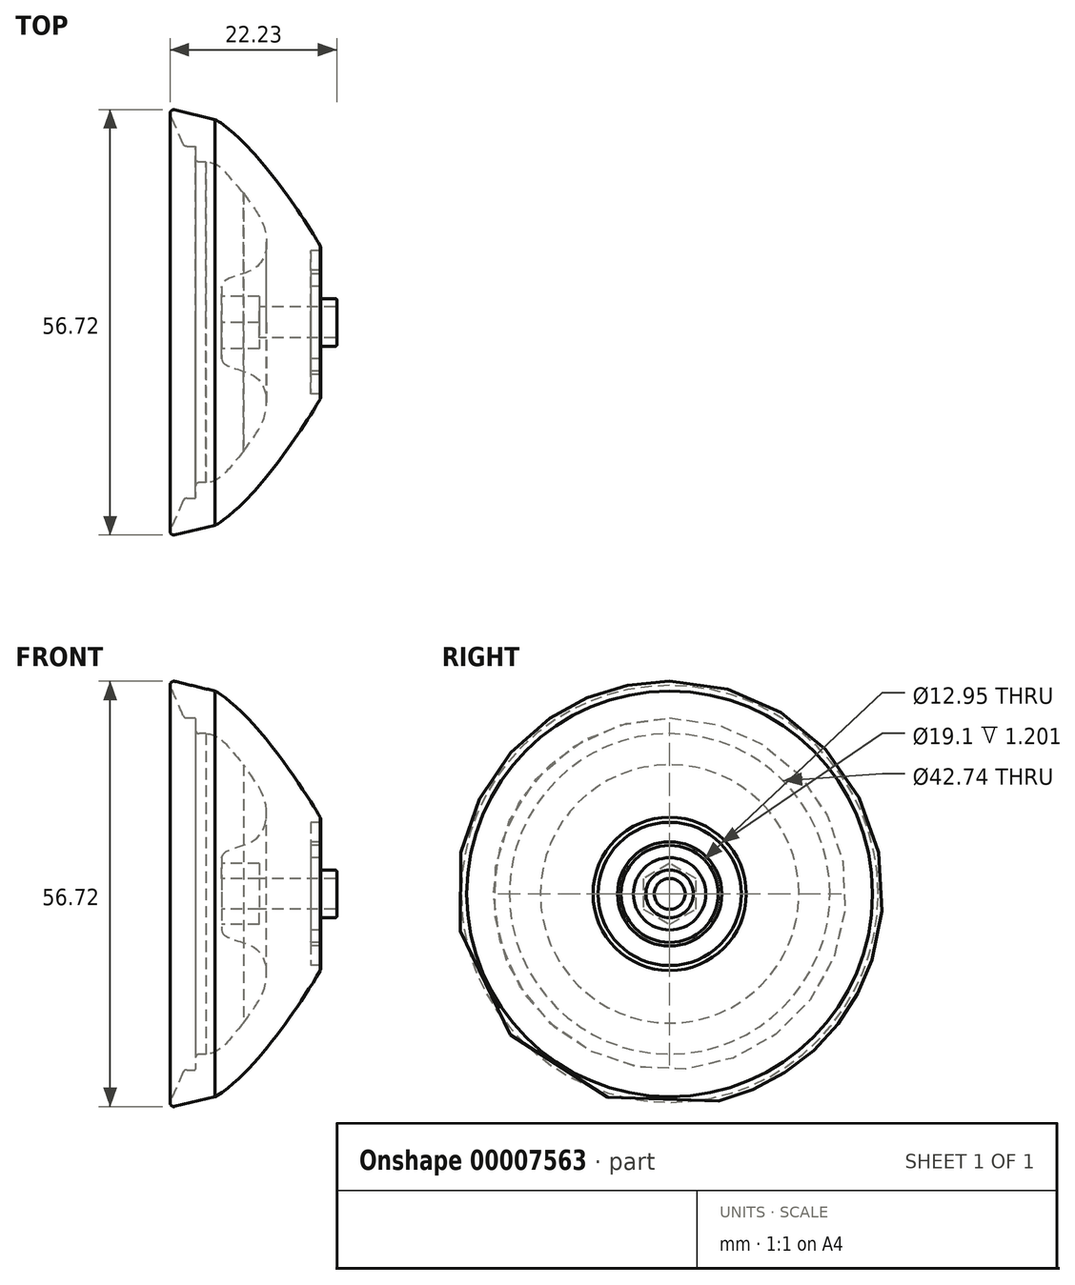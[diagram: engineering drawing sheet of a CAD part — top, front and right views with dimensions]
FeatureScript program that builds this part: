
annotation { "Feature Type Name" : "Feature", "Feature Type Description" : "" }
export const myFeature = defineFeature(function(context is Context, id is Id, definition is map)
    precondition{}
    {
        {
            var Q0;
            Q0=qCreatedBy(makeId("Front.planeOp"),FACE);
            var sketch = newSketch(context, id + "F0", { "sketchPlane" : qUnion([Q0])});
            skLineSegment(sketch, "E0", {"start": v(-27.14, 28.5) * mm, "end": v(36.68, 28.5) * mm, "construction": true});
            skLineSegment(sketch, "E1", {"start": v(20, 42.96) * mm, "end": v(20, -13.53) * mm, "construction": true});
            skLineSegment(sketch, "E2.bottom", {"start": v(22.05, 3.18) * mm, "end": v(20.1, 3.18) * mm});
            skLineSegment(sketch, "E2.left", {"start": v(22.25, 2.98) * mm, "end": v(22.25, 2.25) * mm});
            skLineSegment(sketch, "E3", {"start": v(20, 3.28) * mm, "end": v(20, 4.82) * mm});
            skLineSegment(sketch, "E4", {"start": v(20, 4.82) * mm, "end": v(18.9, 4.82) * mm});
            skLineSegment(sketch, "E5", {"start": v(18.8, 4.92) * mm, "end": v(18.8, 6.38) * mm});
            skLineSegment(sketch, "E6", {"start": v(18.9, 6.48) * mm, "end": v(20, 6.48) * mm});
            skLineSegment(sketch, "E7", {"start": v(20, 6.95) * mm, "end": v(18.8, 6.95) * mm});
            skLineSegment(sketch, "E8", {"start": v(18.8, 6.95) * mm, "end": v(18.8, 9.55) * mm});
            skLineSegment(sketch, "E9", {"start": v(18.8, 9.55) * mm, "end": v(20, 9.55) * mm});
            skLineSegment(sketch, "E10", {"start": v(6.02, 27.05) * mm, "end": v(0.64, 28.35) * mm});
            skLineSegment(sketch, "E11", {"start": v(2.24, 23.47) * mm, "end": v(3.32, 23.47) * mm});
            skLineSegment(sketch, "E12", {"start": v(3.42, 23.37) * mm, "end": v(3.42, 21.87) * mm});
            skLineSegment(sketch, "E13", {"start": v(6.92, 4.84) * mm, "end": v(6.92, 2.25) * mm});
            skLineSegment(sketch, "E14", {"start": v(6.92, 0) * mm, "end": v(6.92, 0) * mm});
            skLineSegment(sketch, "E15", {"start": v(6.92, 0) * mm, "end": v(22.25, 0) * mm});
            skLineSegment(sketch, "E16.top", {"start": v(20.1, 6.48) * mm, "end": v(20.1, 6.48) * mm});
            skLineSegment(sketch, "E16.left", {"start": v(20.1, 6.85) * mm, "end": v(20.1, 6.58) * mm});
            skLineSegment(sketch, "E17.right", {"start": v(20.1, 9.65) * mm, "end": v(20.1, 9.93) * mm});
            skLineSegment(sketch, "E18", {"start": v(3.92, 21.37) * mm, "end": v(4.8, 21.37) * mm});
            skPoint(sketch, "E19.visualSharp", {"position": v(0, 28.5) * mm});
            skArc(sketch, "E19.filletArc", {"start": v(0.64, 28.35) * mm, "mid": v(0.18, 28.23) * mm, "end": v(0.02, 27.8) * mm});
            skPoint(sketch, "E20.visualSharp", {"position": v(20.1, 10.09) * mm});
            skArc(sketch, "E20.filletArc", {"start": v(20.1, 9.93) * mm, "mid": v(20.08, 10.08) * mm, "end": v(20.02, 10.22) * mm});
            skPoint(sketch, "E21.visualSharp", {"position": v(6.92, 5.84) * mm});
            skPoint(sketch, "E22.visualSharp", {"position": v(20.1, 9.55) * mm});
            skArc(sketch, "E22.filletArc", {"start": v(20, 9.55) * mm, "mid": v(20.07, 9.58) * mm, "end": v(20.1, 9.65) * mm});
            skPoint(sketch, "E23.visualSharp", {"position": v(20.1, 6.95) * mm});
            skArc(sketch, "E23.filletArc", {"start": v(20.1, 6.85) * mm, "mid": v(20.07, 6.92) * mm, "end": v(20, 6.95) * mm});
            skPoint(sketch, "E24.visualSharp", {"position": v(20.1, 6.48) * mm});
            skArc(sketch, "E24.filletArc", {"start": v(20, 6.48) * mm, "mid": v(20.07, 6.5) * mm, "end": v(20.1, 6.58) * mm});
            skPoint(sketch, "E25.visualSharp", {"position": v(18.8, 6.48) * mm});
            skArc(sketch, "E25.filletArc", {"start": v(18.9, 6.48) * mm, "mid": v(18.83, 6.45) * mm, "end": v(18.8, 6.38) * mm});
            skPoint(sketch, "E26.visualSharp", {"position": v(18.8, 4.82) * mm});
            skArc(sketch, "E26.filletArc", {"start": v(18.8, 4.92) * mm, "mid": v(18.83, 4.85) * mm, "end": v(18.9, 4.82) * mm});
            skPoint(sketch, "E27.visualSharp", {"position": v(20, 3.18) * mm});
            skArc(sketch, "E27.filletArc", {"start": v(20, 3.28) * mm, "mid": v(20.03, 3.2) * mm, "end": v(20.1, 3.18) * mm});
            skPoint(sketch, "E28.visualSharp", {"position": v(22.25, 3.18) * mm});
            skArc(sketch, "E28.filletArc", {"start": v(22.25, 2.98) * mm, "mid": v(22.2, 3.12) * mm, "end": v(22.05, 3.18) * mm});
            skLineSegment(sketch, "E29", {"start": v(22.05, 2.05) * mm, "end": v(7.12, 2.05) * mm});
            skPoint(sketch, "E30.visualSharp", {"position": v(3.42, 21.37) * mm});
            skArc(sketch, "E30.filletArc", {"start": v(3.42, 21.87) * mm, "mid": v(3.56, 21.52) * mm, "end": v(3.92, 21.37) * mm});
            skPoint(sketch, "E31.visualSharp", {"position": v(22.25, 2.05) * mm});
            skArc(sketch, "E31.filletArc", {"start": v(22.05, 2.05) * mm, "mid": v(22.2, 2.1) * mm, "end": v(22.25, 2.25) * mm});
            skPoint(sketch, "E32.visualSharp", {"position": v(6.92, 2.05) * mm});
            skArc(sketch, "E32.filletArc", {"start": v(6.92, 2.25) * mm, "mid": v(6.98, 2.1) * mm, "end": v(7.12, 2.05) * mm});
            skPoint(sketch, "E33.visualSharp", {"position": v(3.42, 23.47) * mm});
            skArc(sketch, "E33.filletArc", {"start": v(3.42, 23.37) * mm, "mid": v(3.39, 23.44) * mm, "end": v(3.32, 23.47) * mm});
            skFitSpline(sketch, "E34", {"points": [v(6.02, 27.05) * mm, v(10.06, 23.76) * mm, v(17.6, 14.1) * mm, v(20.02, 10.22) * mm], "startDerivative": vector(6.05, -2.38) * mm, "endDerivative": vector(3.82, -7.51) * mm});
            skFitSpline(sketch, "E35", {"points": [v(4.8, 21.37) * mm, v(9.8, 17.23) * mm], "startDerivative": vector(5.8, -0.26) * mm, "endDerivative": vector(6.83, -7.95) * mm});
            skFitSpline(sketch, "E36", {"points": [v(6.92, 4.84) * mm, v(11.26, 7.17) * mm, v(12.82, 11.6) * mm, v(9.8, 17.23) * mm], "startDerivative": vector(0.07, 11.93) * mm, "endDerivative": vector(-14.89, 20.65) * mm});
            skLineSegment(sketch, "E37", {"start": v(0.02, 27.8) * mm, "end": v(1.77, 23.77) * mm});
            skPoint(sketch, "E38.visualSharp", {"position": v(1.9, 23.47) * mm});
            skArc(sketch, "E38.filletArc", {"start": v(1.77, 23.77) * mm, "mid": v(1.96, 23.55) * mm, "end": v(2.24, 23.47) * mm});
            skSolve(sketch);
        }
        {
            var Q0;
            Q0=makeQuery(id+"F0.imprint","IMPRINT",FACE,{"disambiguationData":[TD([[makeQuery(id+"F0.imprint","IMPRINT",EDGE,{"derivedFrom":sQuery(id+"F0.wireOp",EDGE,"E2.bottom")}),1.0]])]});
            var Q1;
            Q1=sQuery(id+"F0.wireOp",EDGE,"E15");
            revolve(context, id + "F1", {"entities" : qUnion([Q0]), "axis" : qUnion([Q1]), "revolveType" : RevolveType.FULL});
        }
        {
            var Q0;
            Q0=makeQuery(id+"F1.opRevolve","SWEPT_FACE",FACE,{"disambiguationData":[OSD([sQuery(id+"F0.wireOp",EDGE,"E13")])]});
            var sketch = newSketch(context, id + "F2", { "sketchPlane" : qUnion([Q0])});
            skCircle(sketch, "E39.cCircle", {"center": v(0, 0) * mm, "radius": 3.5 * mm, "construction": true});
            skLineSegment(sketch, "E39.0", {"start": v(3.5, 2.02) * mm, "end": v(3.5, -2.02) * mm});
            skLineSegment(sketch, "E39.1", {"start": v(3.5, -2.02) * mm, "end": v(0, -4.04) * mm});
            skLineSegment(sketch, "E39.2", {"start": v(0, -4.04) * mm, "end": v(-3.5, -2.02) * mm});
            skLineSegment(sketch, "E39.3", {"start": v(-3.5, -2.02) * mm, "end": v(-3.5, 2.02) * mm});
            skLineSegment(sketch, "E39.4", {"start": v(-3.5, 2.02) * mm, "end": v(0, 4.04) * mm});
            skLineSegment(sketch, "E39.5", {"start": v(0, 4.04) * mm, "end": v(3.5, 2.02) * mm});
            skPoint(sketch, "E39.0.midPoint", {"position": v(3.5, 0) * mm});
            skSolve(sketch);
        }
        {
            var Q0;
            Q0=qSketchRegion(id+"F2",true);
            extrude(context, id + "F3", {"entities" : qUnion([Q0]), "operationType" : NewBodyOperationType.REMOVE, "oppositeDirection" : true, "depth" : 5 * mm});
        }
    });
